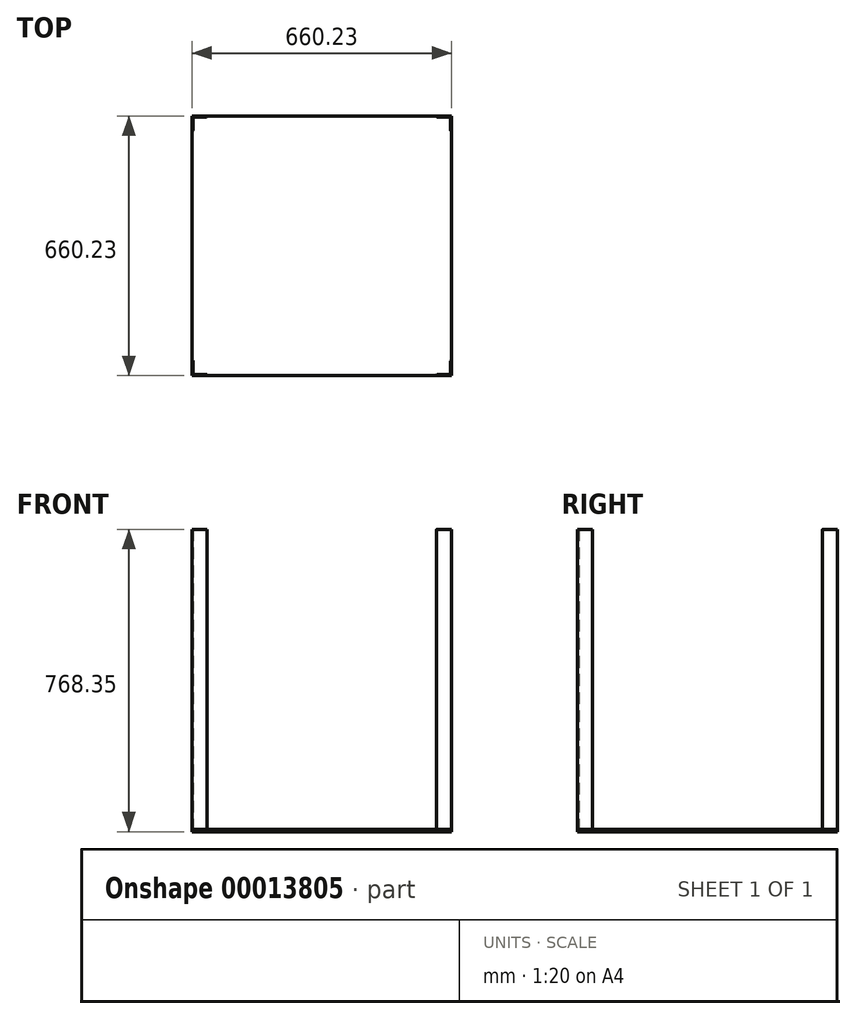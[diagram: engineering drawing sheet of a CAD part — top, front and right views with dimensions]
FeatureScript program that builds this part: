
annotation { "Feature Type Name" : "Feature", "Feature Type Description" : "" }
export const myFeature = defineFeature(function(context is Context, id is Id, definition is map)
    precondition{}
    {
        {
            var Q0;
            Q0=qCreatedBy(makeId("Top.planeOp"),FACE);
            var sketch = newSketch(context, id + "F0", { "sketchPlane" : qUnion([Q0])});
            skLineSegment(sketch, "E0", {"start": v(0, 38.1) * mm, "end": v(0, 0) * mm});
            skLineSegment(sketch, "E1", {"start": v(0, 0) * mm, "end": v(38.1, 0) * mm});
            skLineSegment(sketch, "E2", {"start": v(38.1, 0) * mm, "end": v(38.1, 3.18) * mm});
            skLineSegment(sketch, "E3", {"start": v(38.1, 3.18) * mm, "end": v(3.17, 3.17) * mm});
            skLineSegment(sketch, "E4", {"start": v(3.17, 3.17) * mm, "end": v(3.17, 38.1) * mm});
            skLineSegment(sketch, "E5", {"start": v(3.17, 38.1) * mm, "end": v(0, 38.1) * mm});
            skSolve(sketch);
        }
        {
            var Q0;
            Q0 = qSketchRegion(id + "F0", true);
            extrude(context, id + "F1", {"entities" : qUnion([Q0]), "depth" : 762 * mm});
        }
        {
            var Q0;
            Q0=makeQuery(id+"F1.opExtrude","CAP_VERTEX",VERTEX,{"disambiguationData":[OSD([sQuery(id+"F0.wireOp",EDGE,"E3"),sQuery(id+"F0.wireOp",EDGE,"E4")])],"isStart":true});
            var Q1;
            Q1=makeQuery(id+"F1.opExtrude","CAP_VERTEX",VERTEX,{"disambiguationData":[OSD([sQuery(id+"F0.wireOp",EDGE,"E0"),sQuery(id+"F0.wireOp",EDGE,"E1")])],"isStart":true});
            var Q2;
            Q2=makeQuery(id+"F1.opExtrude","CAP_VERTEX",VERTEX,{"disambiguationData":[OSD([sQuery(id+"F0.wireOp",EDGE,"E0"),sQuery(id+"F0.wireOp",EDGE,"E1")])],"isStart":false});
            cPlane(context, id + "F2", {"entities" : qUnion([Q0, Q1, Q2]), "cplaneType" : CPlaneType.THREE_POINT, "offset" : 152.4 * mm, "width" : 152.4 * mm, "height" : 152.4 * mm});
        }
        {
            var Q0;
            Q0=qCreatedBy(id+"F2.planeOp",FACE);
            var sketch = newSketch(context, id + "F3", { "sketchPlane" : qUnion([Q0])});
            skLineSegment(sketch, "E6.0", {"start": v(0, 762) * mm, "end": v(0, 0) * mm});
            skLineSegment(sketch, "E7", {"start": v(466.85, 0) * mm, "end": v(466.85, 286.4) * mm, "construction": true});
            skSolve(sketch);
        }
        {
            var Q0;
            Q0=makeQuery(id+"F1.opExtrude","SWEPT_BODY",BODY,{"disambiguationData":[OSD([sQuery(id+"F0.wireOp",EDGE,"E0"),sQuery(id+"F0.wireOp",EDGE,"E1"),sQuery(id+"F0.wireOp",EDGE,"E2"),sQuery(id+"F0.wireOp",EDGE,"E3"),sQuery(id+"F0.wireOp",EDGE,"E4"),sQuery(id+"F0.wireOp",EDGE,"E5")])]});
            var Q1;
            Q1=sQuery(id+"F3.wireOp",EDGE,"E7");
            circularPattern(context, id + "F4", {"entities" : qUnion([Q0]), "axis" : qUnion([Q1]), "angle" : 90 * degree, "instanceCount" : 4});
        }
        {
            var Q0;
            Q0=makeQuery(id+"F1.opExtrude","CAP_FACE",FACE,{"disambiguationData":[OSD([sQuery(id+"F0.wireOp",EDGE,"E0"),sQuery(id+"F0.wireOp",EDGE,"E1"),sQuery(id+"F0.wireOp",EDGE,"E2"),sQuery(id+"F0.wireOp",EDGE,"E3"),sQuery(id+"F0.wireOp",EDGE,"E4"),sQuery(id+"F0.wireOp",EDGE,"E5")])],"isStart":true});
            var sketch = newSketch(context, id + "F5", { "sketchPlane" : qUnion([Q0])});
            skLineSegment(sketch, "E8.0.0", {"start": v(660.23, -622.13) * mm, "end": v(657.05, -622.13) * mm});
            skLineSegment(sketch, "E8.0.1", {"start": v(657.05, -622.13) * mm, "end": v(657.05, -657.05) * mm});
            skLineSegment(sketch, "E8.0.2", {"start": v(657.05, -657.05) * mm, "end": v(622.13, -657.05) * mm});
            skLineSegment(sketch, "E8.0.3", {"start": v(622.13, -657.05) * mm, "end": v(622.13, -660.23) * mm});
            skLineSegment(sketch, "E8.0.4", {"start": v(622.13, -660.23) * mm, "end": v(660.23, -660.23) * mm});
            skLineSegment(sketch, "E8.0.5", {"start": v(660.23, -660.23) * mm, "end": v(660.23, -622.13) * mm});
            skLineSegment(sketch, "E9.bottom", {"start": v(0, 0) * mm, "end": v(660.23, 0) * mm});
            skLineSegment(sketch, "E9.top", {"start": v(0, -660.23) * mm, "end": v(660.23, -660.23) * mm});
            skLineSegment(sketch, "E9.left", {"start": v(0, 0) * mm, "end": v(0, -660.23) * mm});
            skLineSegment(sketch, "E9.right", {"start": v(660.23, 0) * mm, "end": v(660.23, -660.23) * mm});
            skSolve(sketch);
        }
        {
            var Q0;
            Q0 = qSketchRegion(id + "F5", true);
            extrude(context, id + "F6", {"entities" : qUnion([Q0]), "depth" : 6.35 * mm});
        }
        {
            var Q0;
            Q0=makeQuery(id+"F4.opPattern","COPY",EDGE,{"derivedFrom":makeQuery(id+"F1.opExtrude","SWEPT_EDGE",EDGE,{"disambiguationData":[OSD([sQuery(id+"F0.wireOp",EDGE,"E3"),sQuery(id+"F0.wireOp",EDGE,"E4")])]}),"instanceName":"3"});
            var Q1;
            Q1=makeQuery(id+"F1.opExtrude","SWEPT_EDGE",EDGE,{"disambiguationData":[OSD([sQuery(id+"F0.wireOp",EDGE,"E3"),sQuery(id+"F0.wireOp",EDGE,"E4")])]});
            var Q2;
            Q2=makeQuery(id+"F4.opPattern","COPY",EDGE,{"derivedFrom":makeQuery(id+"F1.opExtrude","SWEPT_EDGE",EDGE,{"disambiguationData":[OSD([sQuery(id+"F0.wireOp",EDGE,"E3"),sQuery(id+"F0.wireOp",EDGE,"E4")])]}),"instanceName":"1"});
            var Q3;
            Q3=makeQuery(id+"F4.opPattern","COPY",EDGE,{"derivedFrom":makeQuery(id+"F1.opExtrude","SWEPT_EDGE",EDGE,{"disambiguationData":[OSD([sQuery(id+"F0.wireOp",EDGE,"E3"),sQuery(id+"F0.wireOp",EDGE,"E4")])]}),"instanceName":"2"});
            fillet(context, id + "F7", {"entities" : qUnion([Q0, Q1, Q2, Q3]), "radius" : 5.08 * mm, "tangentPropagation" : true, "allowEdgeOverflow" : false});
        }
        {
            var Q0;
            Q0=makeQuery(id+"F4.opPattern","COPY",EDGE,{"derivedFrom":makeQuery(id+"F1.opExtrude","SWEPT_EDGE",EDGE,{"disambiguationData":[OSD([sQuery(id+"F0.wireOp",EDGE,"E0"),sQuery(id+"F0.wireOp",EDGE,"E5")])]}),"instanceName":"1"});
            var Q1;
            Q1=makeQuery(id+"F4.opPattern","COPY",EDGE,{"derivedFrom":makeQuery(id+"F1.opExtrude","SWEPT_EDGE",EDGE,{"disambiguationData":[OSD([sQuery(id+"F0.wireOp",EDGE,"E4"),sQuery(id+"F0.wireOp",EDGE,"E5")])]}),"instanceName":"1"});
            var Q2;
            Q2=makeQuery(id+"F4.opPattern","COPY",EDGE,{"derivedFrom":makeQuery(id+"F1.opExtrude","SWEPT_EDGE",EDGE,{"disambiguationData":[OSD([sQuery(id+"F0.wireOp",EDGE,"E2"),sQuery(id+"F0.wireOp",EDGE,"E3")])]}),"instanceName":"1"});
            var Q3;
            Q3=makeQuery(id+"F4.opPattern","COPY",EDGE,{"derivedFrom":makeQuery(id+"F1.opExtrude","SWEPT_EDGE",EDGE,{"disambiguationData":[OSD([sQuery(id+"F0.wireOp",EDGE,"E1"),sQuery(id+"F0.wireOp",EDGE,"E2")])]}),"instanceName":"1"});
            var Q4;
            Q4=makeQuery(id+"F4.opPattern","COPY",EDGE,{"derivedFrom":makeQuery(id+"F1.opExtrude","SWEPT_EDGE",EDGE,{"disambiguationData":[OSD([sQuery(id+"F0.wireOp",EDGE,"E1"),sQuery(id+"F0.wireOp",EDGE,"E2")])]}),"instanceName":"2"});
            var Q5;
            Q5=makeQuery(id+"F4.opPattern","COPY",EDGE,{"derivedFrom":makeQuery(id+"F1.opExtrude","SWEPT_EDGE",EDGE,{"disambiguationData":[OSD([sQuery(id+"F0.wireOp",EDGE,"E2"),sQuery(id+"F0.wireOp",EDGE,"E3")])]}),"instanceName":"2"});
            var Q6;
            Q6=makeQuery(id+"F4.opPattern","COPY",EDGE,{"derivedFrom":makeQuery(id+"F1.opExtrude","SWEPT_EDGE",EDGE,{"disambiguationData":[OSD([sQuery(id+"F0.wireOp",EDGE,"E4"),sQuery(id+"F0.wireOp",EDGE,"E5")])]}),"instanceName":"2"});
            var Q7;
            Q7=makeQuery(id+"F4.opPattern","COPY",EDGE,{"derivedFrom":makeQuery(id+"F1.opExtrude","SWEPT_EDGE",EDGE,{"disambiguationData":[OSD([sQuery(id+"F0.wireOp",EDGE,"E0"),sQuery(id+"F0.wireOp",EDGE,"E5")])]}),"instanceName":"2"});
            var Q8;
            Q8=makeQuery(id+"F4.opPattern","COPY",EDGE,{"derivedFrom":makeQuery(id+"F1.opExtrude","SWEPT_EDGE",EDGE,{"disambiguationData":[OSD([sQuery(id+"F0.wireOp",EDGE,"E1"),sQuery(id+"F0.wireOp",EDGE,"E2")])]}),"instanceName":"3"});
            var Q9;
            Q9=makeQuery(id+"F4.opPattern","COPY",EDGE,{"derivedFrom":makeQuery(id+"F1.opExtrude","SWEPT_EDGE",EDGE,{"disambiguationData":[OSD([sQuery(id+"F0.wireOp",EDGE,"E2"),sQuery(id+"F0.wireOp",EDGE,"E3")])]}),"instanceName":"3"});
            var Q10;
            Q10=makeQuery(id+"F4.opPattern","COPY",EDGE,{"derivedFrom":makeQuery(id+"F1.opExtrude","SWEPT_EDGE",EDGE,{"disambiguationData":[OSD([sQuery(id+"F0.wireOp",EDGE,"E4"),sQuery(id+"F0.wireOp",EDGE,"E5")])]}),"instanceName":"3"});
            var Q11;
            Q11=makeQuery(id+"F4.opPattern","COPY",EDGE,{"derivedFrom":makeQuery(id+"F1.opExtrude","SWEPT_EDGE",EDGE,{"disambiguationData":[OSD([sQuery(id+"F0.wireOp",EDGE,"E0"),sQuery(id+"F0.wireOp",EDGE,"E5")])]}),"instanceName":"3"});
            var Q12;
            Q12=makeQuery(id+"F1.opExtrude","SWEPT_EDGE",EDGE,{"disambiguationData":[OSD([sQuery(id+"F0.wireOp",EDGE,"E1"),sQuery(id+"F0.wireOp",EDGE,"E2")])]});
            var Q13;
            Q13=makeQuery(id+"F1.opExtrude","SWEPT_EDGE",EDGE,{"disambiguationData":[OSD([sQuery(id+"F0.wireOp",EDGE,"E2"),sQuery(id+"F0.wireOp",EDGE,"E3")])]});
            var Q14;
            Q14=makeQuery(id+"F1.opExtrude","SWEPT_EDGE",EDGE,{"disambiguationData":[OSD([sQuery(id+"F0.wireOp",EDGE,"E0"),sQuery(id+"F0.wireOp",EDGE,"E5")])]});
            var Q15;
            Q15=makeQuery(id+"F1.opExtrude","SWEPT_EDGE",EDGE,{"disambiguationData":[OSD([sQuery(id+"F0.wireOp",EDGE,"E4"),sQuery(id+"F0.wireOp",EDGE,"E5")])]});
            fillet(context, id + "F8", {"entities" : qUnion([Q0, Q1, Q2, Q3, Q4, Q5, Q6, Q7, Q8, Q9, Q10, Q11, Q12, Q13, Q14, Q15]), "radius" : 1.27 * mm, "tangentPropagation" : true, "allowEdgeOverflow" : false});
        }
    });
